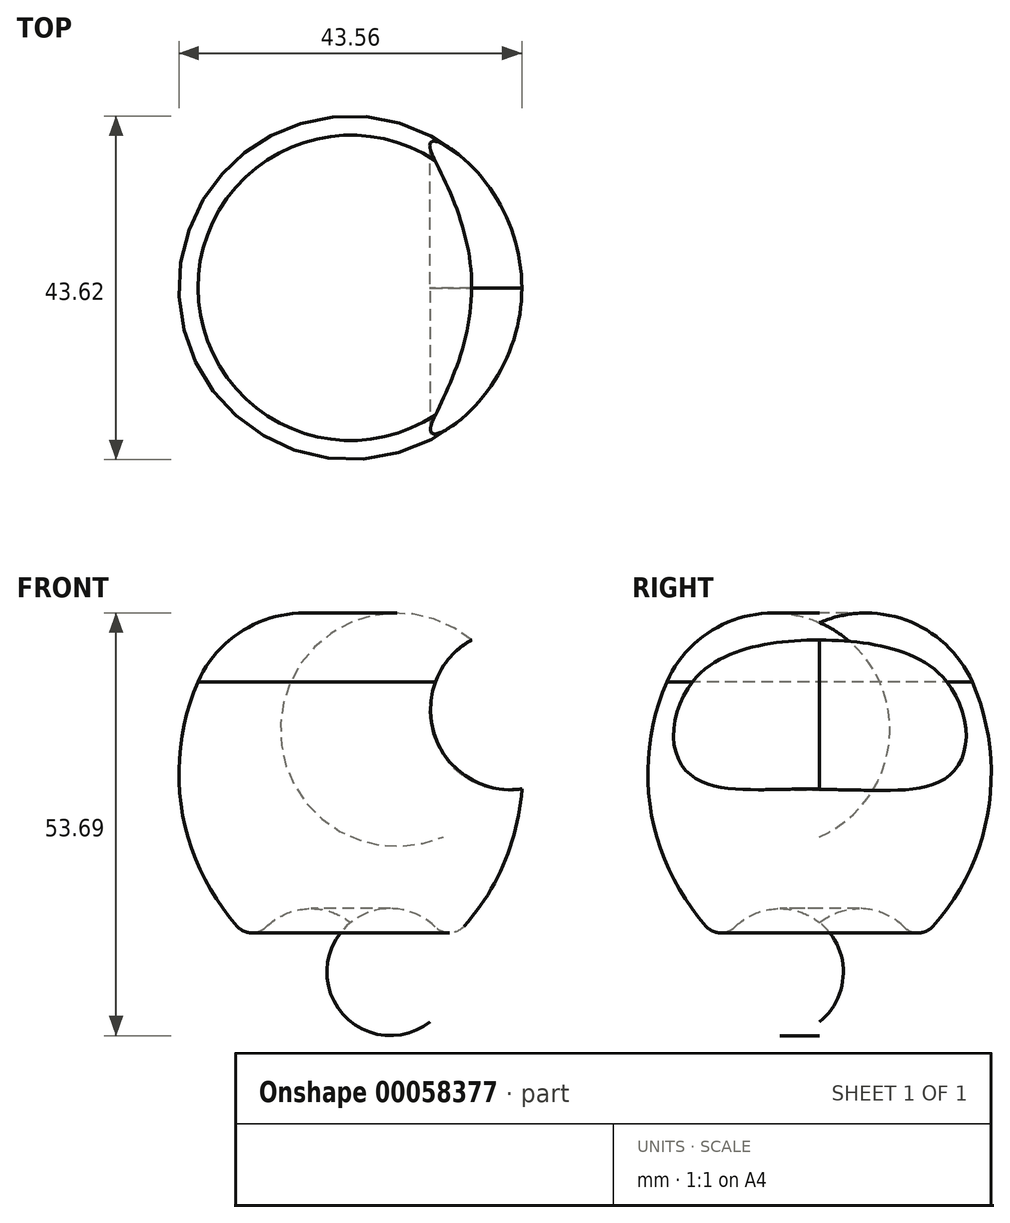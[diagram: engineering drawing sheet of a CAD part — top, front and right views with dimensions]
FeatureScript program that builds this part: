
annotation { "Feature Type Name" : "Feature", "Feature Type Description" : "" }
export const myFeature = defineFeature(function(context is Context, id is Id, definition is map)
    precondition{}
    {
        {
            var Q0;
            Q0=qCreatedBy(makeId("Front.planeOp"),FACE);
            var sketch = newSketch(context, id + "F0", { "sketchPlane" : qUnion([Q0])});
            skArc(sketch, "E0", {"start": v(-11.35, -18.08) * mm, "mid": v(-11.8, -18.07) * mm, "end": v(-12.25, -18.08) * mm});
            skArc(sketch, "E1", {"start": v(0, -15.42) * mm, "mid": v(-6.76, -13.83) * mm, "end": v(-12.25, -18.08) * mm});
            skLineSegment(sketch, "E2", {"start": v(0, 22.68) * mm, "end": v(0, -15.42) * mm});
            skArc(sketch, "E3", {"start": v(-19.4, 15.17) * mm, "mid": v(-21.16, -2.6) * mm, "end": v(-12.25, -18.08) * mm});
            skArc(sketch, "E4", {"start": v(0, 22.68) * mm, "mid": v(-11.63, 22.74) * mm, "end": v(-19.72, 14.4) * mm});
            skPoint(sketch, "E5.orphan", {"position": v(-14.67, 22.68) * mm});
            skSolve(sketch);
        }
        {
            var Q0;
            Q0=makeQuery(id+"F0.imprint","IMPRINT",FACE,{"disambiguationData":[TD([[makeQuery(id+"F0.imprint","IMPRINT",EDGE,{"derivedFrom":sQuery(id+"F0.wireOp",EDGE,"0e42afe3-a82f-4356-9a18-ff2c233b2854")}),1.0]])]});
            var Q1;
            Q1=makeQuery(id+"F0.imprint","IMPRINT",FACE,{"disambiguationData":[TD([[makeQuery(id+"F0.imprint","IMPRINT",EDGE,{"derivedFrom":sQuery(id+"F0.wireOp",EDGE,"f4b8eed6-12df-4d4f-bd6f-74d1f474a73e")}),1.0]])]});
            var Q2;
            {var subQ1=sQuery(id+"F0.wireOp",EDGE,"E1");Q2=makeQuery(id+"F0.imprint","IMPRINT",FACE,{"disambiguationData":[TD([[makeQuery(id+"F0.imprint","IMPRINT",EDGE,{"derivedFrom":subQ1}),-1.0]])]});}
            var Q3;
            Q3=sQuery(id+"F0.wireOp",EDGE,"E2");
            revolve(context, id + "F1", {"entities" : qUnion([Q0, Q1, Q2]), "axis" : qUnion([Q3]), "revolveType" : RevolveType.FULL});
        }
        {
            var Q0;
            Q0=qCreatedBy(makeId("Front.planeOp"),FACE);
            var sketch = newSketch(context, id + "F2", { "sketchPlane" : qUnion([Q0])});
            skCircle(sketch, "E6", {"center": v(20.2, 11.52) * mm, "radius": 10.16 * mm});
            skSolve(sketch);
        }
        {
            var Q0;
            Q0=makeQuery(id+"F2.imprint","IMPRINT",FACE,{"disambiguationData":[TD([[makeQuery(id+"F2.imprint","IMPRINT",EDGE,{"derivedFrom":sQuery(id+"F2.wireOp",EDGE,"E6")}),1.0]])]});
            extrude(context, id + "F3", {"entities" : qUnion([Q0]), "operationType" : NewBodyOperationType.REMOVE, "endBound" : BoundingType.THROUGH_ALL, "oppositeDirection" : true, "depth" : 25.4 * mm});
        }
        {
            var Q0;
            Q0=makeQuery(id+"F1.opRevolve","SWEPT_EDGE",EDGE,{"disambiguationData":[OSD([sQuery(id+"F0.wireOp",EDGE,"E1"),sQuery(id+"F0.wireOp",EDGE,"E3")])]});
            fillet(context, id + "F4", {"entities" : qUnion([Q0]), "radius" : 2.54 * mm, "tangentPropagation" : true, "allowEdgeOverflow" : false});
        }
        {
            var Q0;
            Q0=qCreatedBy(makeId("Front.planeOp"),FACE);
            var sketch = newSketch(context, id + "F5", { "sketchPlane" : qUnion([Q0])});
            skCircle(sketch, "E7", {"center": v(20.3, 11.62) * mm, "radius": 10.16 * mm});
            skSolve(sketch);
        }
        {
            var Q0;
            Q0=makeQuery(id+"F5.imprint","IMPRINT",FACE,{"disambiguationData":[TD([[makeQuery(id+"F5.imprint","IMPRINT",EDGE,{"derivedFrom":sQuery(id+"F5.wireOp",EDGE,"E7")}),1.0]])]});
            extrude(context, id + "F6", {"entities" : qUnion([Q0]), "operationType" : NewBodyOperationType.REMOVE, "endBound" : BoundingType.THROUGH_ALL, "depth" : 25.4 * mm});
        }
    });
